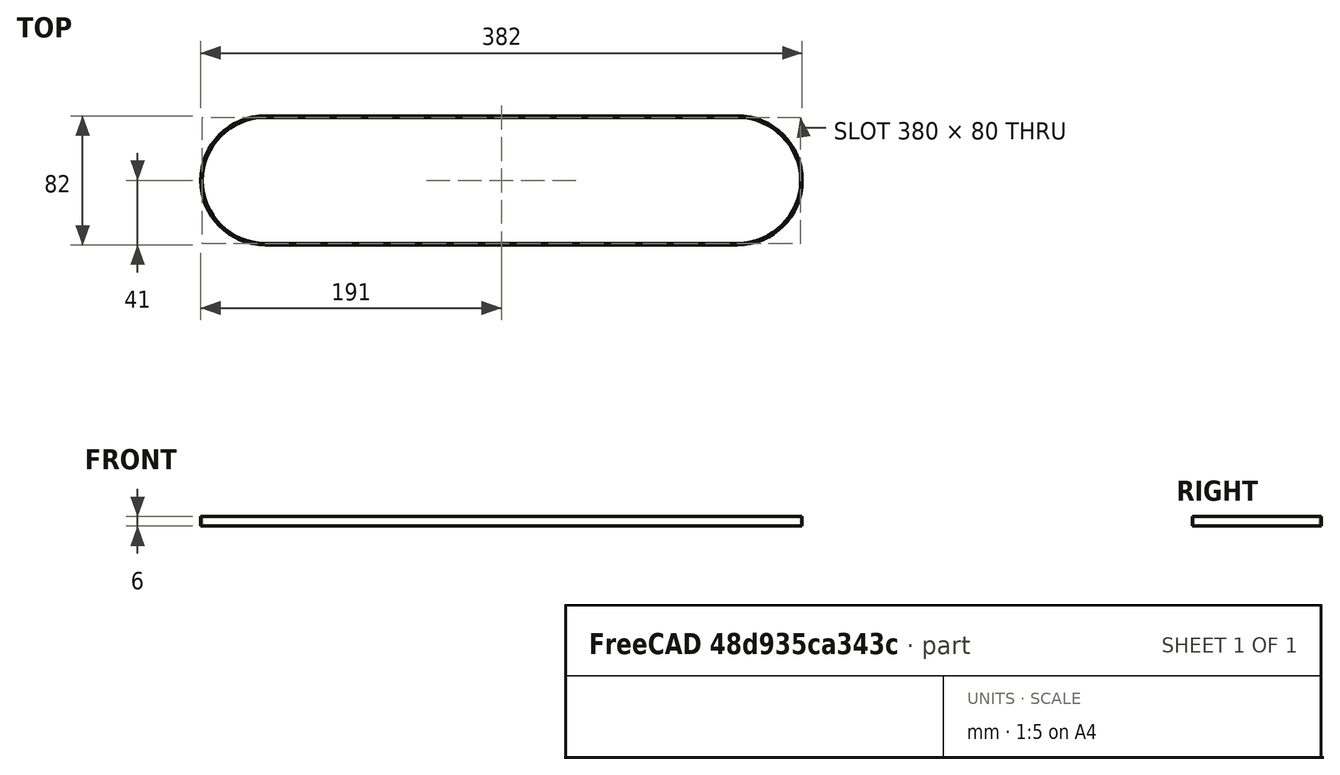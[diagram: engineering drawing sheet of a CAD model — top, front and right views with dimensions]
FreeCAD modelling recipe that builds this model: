
FCSTD DOCUMENT  (FreeCAD 0.19R24276 (Git))
Label: belt
License: All rights reserved
LicenseURL: http://en.wikipedia.org/wiki/All_rights_reserved
objects: Sketcher::SketchObject×1, PartDesign::Pad×1, PartDesign::Body×1
note: 4 computed .brp shape members not serialized (recipe doc carries the construction recipe); baked Part::Feature solids carry a one-line shape summary decoded from their .brp

FEATURE [Sketcher::SketchObject] Sketch
  FullyConstrained = true
  MapMode = 5
  Support = -> [XY_Plane]
  sketch-geometry (14):
    g0: ArcOfCircle CenterX=0 CenterY=0 CenterZ=0 NormalX=0 NormalY=0 NormalZ=1 AngleXU=0 Radius=41 StartAngle=1.5708 EndAngle=4.71239
    g1: ArcOfCircle CenterX=300 CenterY=0 CenterZ=0 NormalX=0 NormalY=0 NormalZ=1 AngleXU=0 Radius=41 StartAngle=4.71239 EndAngle=7.85398
    g2: LineSegment StartX=2.5e-15 StartY=41 StartZ=0 EndX=300 EndY=41 EndZ=0
    g3: LineSegment StartX=300 StartY=-41 StartZ=0 EndX=0 EndY=-41 EndZ=0
    g4: LineSegment StartX=300 StartY=0 StartZ=0 EndX=300 EndY=-41 EndZ=0
    g5: LineSegment StartX=0 StartY=0 StartZ=0 EndX=0 EndY=-41 EndZ=0
    g6: LineSegment StartX=2.5e-15 StartY=0 StartZ=0 EndX=2.5e-15 EndY=41 EndZ=0
    g7: ArcOfCircle CenterX=0 CenterY=0 CenterZ=0 NormalX=0 NormalY=0 NormalZ=1 AngleXU=0 Radius=40 StartAngle=1.5708 EndAngle=4.71239
    g8: ArcOfCircle CenterX=300 CenterY=0 CenterZ=0 NormalX=0 NormalY=0 NormalZ=1 AngleXU=0 Radius=40 StartAngle=4.71239 EndAngle=7.85398
    g9: LineSegment StartX=0 StartY=40 StartZ=0 EndX=300 EndY=40 EndZ=0
    g10: LineSegment StartX=0 StartY=-40 StartZ=0 EndX=300 EndY=-40 EndZ=0
    g11: LineSegment StartX=300 StartY=0 StartZ=0 EndX=300 EndY=-40 EndZ=0
    g12: LineSegment StartX=0 StartY=0 StartZ=0 EndX=0 EndY=-40 EndZ=0
    g13: LineSegment StartX=0 StartY=0 StartZ=0 EndX=0 EndY=40 EndZ=0
  constraints (39):
    c: Coincident(g0,g-1)
    c: PointOnObject(g1,g-1)
    c: DistanceX(g-1,g1) = 300
    c: Diameter(g0) = 82
    c: Diameter(g1) = 82
    c: Horizontal(g2)
    c: Horizontal(g3)
    c: Coincident(g4,g1)
    c: Coincident(g4,g3)
    c: Coincident(g5,g-1)
    c: Coincident(g5,g3)
    c: Coincident(g6,g-1)
    c: Coincident(g6,g2)
    c: Vertical(g6)
    c: Vertical(g5)
    c: Coincident(g0,g2)
    c: Coincident(g0,g3)
    c: Coincident(g1,g3)
    c: Coincident(g1,g2)
    c: Coincident(g7,g-1)
    c: Coincident(g8,g1)
    c: Equal(g7,g8)
    c: PointOnObject(g9,g7)
    c: Horizontal(g9)
    c: PointOnObject(g10,g7)
    c: Horizontal(g10)
    c: Coincident(g11,g1)
    c: Coincident(g11,g10)
    c: Coincident(g12,g-1)
    c: Coincident(g12,g10)
    c: Coincident(g13,g-1)
    c: Coincident(g13,g9)
    c: Vertical(g13)
    c: Vertical(g12)
    c: PointOnObject(g7,g6)
    c: PointOnObject(g7,g5)
    c: Coincident(g8,g10)
    c: Coincident(g8,g9)
    c: Diameter(g8) = 80
FEATURE [PartDesign::Pad] Pad
  Direction = (1,1,1)
  Length = 6
  Length2 = 100
  Profile = -> Sketch
  Type = 0
FEATURE [PartDesign::Body] Body
  Group = -> [Sketch,Pad]
  Origin = -> Origin
  Tip = -> Pad
